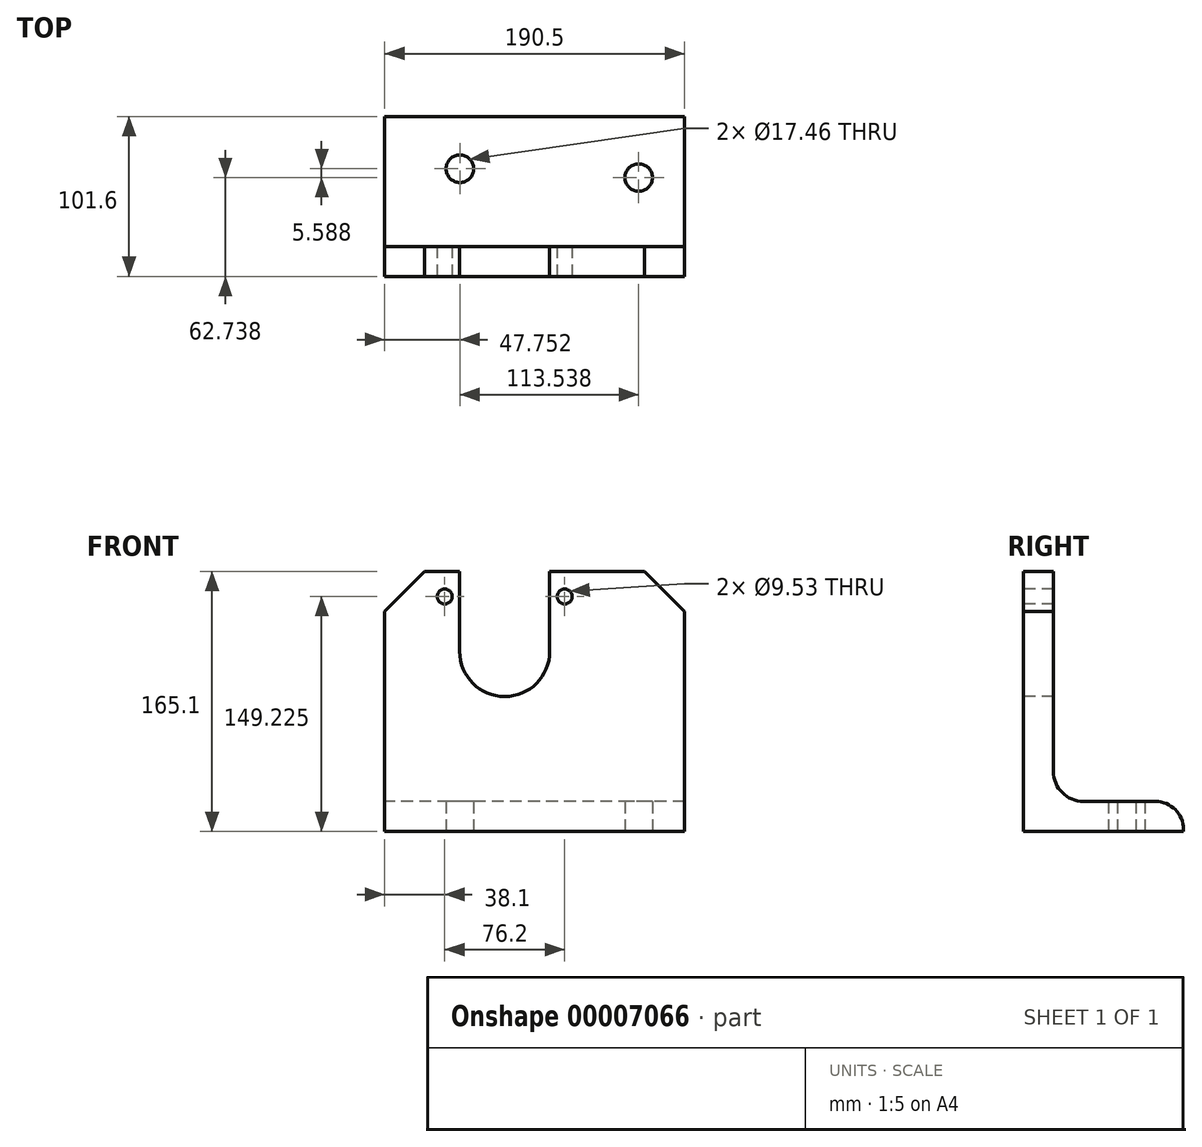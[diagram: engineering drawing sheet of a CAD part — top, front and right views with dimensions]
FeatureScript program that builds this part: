
annotation { "Feature Type Name" : "Feature", "Feature Type Description" : "" }
export const myFeature = defineFeature(function(context is Context, id is Id, definition is map)
    precondition{}
    {
        {
            var Q0;
            Q0=qCreatedBy(makeId("Right.planeOp"),FACE);
            var sketch = newSketch(context, id + "F0", { "sketchPlane" : qUnion([Q0])});
            skLineSegment(sketch, "E0", {"start": v(0, 0) * mm, "end": v(0, 165.1) * mm});
            skLineSegment(sketch, "E1", {"start": v(0, 0) * mm, "end": v(101.6, 0) * mm});
            skLineSegment(sketch, "E2.0", {"start": v(19.05, 38.1) * mm, "end": v(19.05, 165.1) * mm});
            skLineSegment(sketch, "E3.0", {"start": v(38.1, 19.05) * mm, "end": v(83.82, 19.05) * mm});
            skArc(sketch, "E4.filletArc", {"start": v(19.05, 38.1) * mm, "mid": v(24.63, 24.63) * mm, "end": v(38.1, 19.05) * mm});
            skLineSegment(sketch, "E5", {"start": v(101.6, 1.27) * mm, "end": v(101.6, 0) * mm});
            skPoint(sketch, "E6.visualSharp", {"position": v(101.6, 19.05) * mm});
            skArc(sketch, "E6.filletArc", {"start": v(101.6, 1.27) * mm, "mid": v(96.4, 13.84) * mm, "end": v(83.82, 19.05) * mm});
            skLineSegment(sketch, "E7", {"start": v(0, 165.1) * mm, "end": v(19.05, 165.1) * mm});
            skSolve(sketch);
        }
        {
            var Q0;
            Q0 = qSketchRegion(id + "F0", true);
            extrude(context, id + "F1", {"entities" : qUnion([Q0]), "endBound" : BoundingType.SYMMETRIC, "depth" : 190.5 * mm});
        }
        {
            var Q0;
            Q0=makeQuery(id+"F1.opExtrude","SWEPT_FACE",FACE,{"disambiguationData":[OSD([sQuery(id+"F0.wireOp",EDGE,"E0")])]});
            var sketch = newSketch(context, id + "F2", { "sketchPlane" : qUnion([Q0])});
            skLineSegment(sketch, "E8.0", {"start": v(-19.05, 0) * mm, "end": v(-19.05, 165.1) * mm, "construction": true});
            skLineSegment(sketch, "E9.0", {"start": v(95.25, 114.3) * mm, "end": v(-95.25, 114.3) * mm, "construction": true});
            skArc(sketch, "E10", {"start": v(-47.63, 114.3) * mm, "mid": v(-19.05, 85.73) * mm, "end": v(9.52, 114.3) * mm});
            skLineSegment(sketch, "E11", {"start": v(-47.63, 114.3) * mm, "end": v(-47.63, 184.37) * mm});
            skLineSegment(sketch, "E12.0.MirrorCS", {"start": v(9.52, 114.3) * mm, "end": v(9.52, 184.37) * mm});
            skLineSegment(sketch, "E13", {"start": v(-47.63, 184.37) * mm, "end": v(9.52, 184.37) * mm});
            skSolve(sketch);
        }
        {
            var Q0;
            Q0 = qSketchRegion(id + "F2", true);
            extrude(context, id + "F3", {"entities" : qUnion([Q0]), "operationType" : NewBodyOperationType.REMOVE, "endBound" : BoundingType.THROUGH_ALL, "oppositeDirection" : true, "depth" : 25.4 * mm});
        }
        {
            var Q0;
            Q0=makeQuery(id+"F1.opExtrude","CAP_EDGE",EDGE,{"disambiguationData":[OSD([sQuery(id+"F0.wireOp",EDGE,"E7")])],"isStart":true});
            var Q1;
            Q1=makeQuery(id+"F1.opExtrude","CAP_EDGE",EDGE,{"disambiguationData":[OSD([sQuery(id+"F0.wireOp",EDGE,"E7")])],"isStart":false});
            chamfer(context, id + "F4", {"entities" : qUnion([Q0, Q1]), "width" : 25.4 * mm, "tangentPropagation" : true});
        }
        {
            var Q0;
            Q0=makeQuery(id+"F1.opExtrude","SWEPT_FACE",FACE,{"disambiguationData":[OSD([sQuery(id+"F0.wireOp",EDGE,"E0")])]});
            var sketch = newSketch(context, id + "F5", { "sketchPlane" : qUnion([Q0])});
            skLineSegment(sketch, "E14.0", {"start": v(95.25, 149.23) * mm, "end": v(-95.25, 149.23) * mm, "construction": true});
            skLineSegment(sketch, "E15.0", {"start": v(19.05, 0) * mm, "end": v(19.05, 165.1) * mm, "construction": true});
            skCircle(sketch, "E16", {"center": v(19.05, 149.23) * mm, "radius": 4.76 * mm});
            skLineSegment(sketch, "E17.0", {"start": v(-57.15, 0) * mm, "end": v(-57.15, 165.1) * mm, "construction": true});
            skCircle(sketch, "E18", {"center": v(-57.15, 149.23) * mm, "radius": 4.76 * mm});
            skSolve(sketch);
        }
        {
            var Q0;
            Q0 = qSketchRegion(id + "F5", true);
            extrude(context, id + "F6", {"entities" : qUnion([Q0]), "operationType" : NewBodyOperationType.REMOVE, "endBound" : BoundingType.THROUGH_ALL, "oppositeDirection" : true, "depth" : 25.4 * mm});
        }
        {
            var Q0;
            Q0=makeQuery(id+"F1.opExtrude","SWEPT_FACE",FACE,{"disambiguationData":[OSD([sQuery(id+"F0.wireOp",EDGE,"E1")])]});
            var sketch = newSketch(context, id + "F7", { "sketchPlane" : qUnion([Q0])});
            skLineSegment(sketch, "E19.0", {"start": v(-47.5, 0) * mm, "end": v(-47.5, -101.6) * mm, "construction": true});
            skLineSegment(sketch, "E20.0", {"start": v(66.04, 0) * mm, "end": v(66.04, -101.6) * mm, "construction": true});
            skLineSegment(sketch, "E21.0", {"start": v(95.25, -68.33) * mm, "end": v(-95.25, -68.33) * mm, "construction": true});
            skCircle(sketch, "E22", {"center": v(-47.5, -68.33) * mm, "radius": 8.73 * mm});
            skLineSegment(sketch, "E23.0", {"start": v(95.25, -62.74) * mm, "end": v(-95.25, -62.74) * mm, "construction": true});
            skCircle(sketch, "E24", {"center": v(66.04, -62.74) * mm, "radius": 8.73 * mm});
            skSolve(sketch);
        }
        {
            var Q0;
            Q0 = qSketchRegion(id + "F7", true);
            extrude(context, id + "F8", {"entities" : qUnion([Q0]), "operationType" : NewBodyOperationType.REMOVE, "endBound" : BoundingType.THROUGH_ALL, "oppositeDirection" : true, "depth" : 25.4 * mm});
        }
    });
